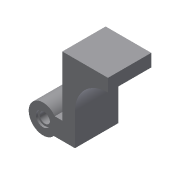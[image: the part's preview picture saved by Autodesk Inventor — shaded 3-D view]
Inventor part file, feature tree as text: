
AUTODESK INVENTOR PART (.ipt)
format: ipt  version: 2015 (Build 190159000, 159)  size: 150,016 bytes
history: native  units: in
note: dims shown in document units (in); Inventor stores cm internally (conversion verified against a paired STEP export)
features: extrude x6, sketch x6, mirror x2, projected_geometry x2, fillet x1, reference x1
ambient origin geometry x8: Origin, YZ Plane, XZ Plane, XY Plane, X Axis, Y Axis, Z Axis, Center Point
bodies: Solid1 (feature_tree)
feature tree (18):
  extrude  "Extrusion1"  Depth=0.9375in TaperAngle=0.0deg
  extrude  "Extrusion2"  Depth=0.4882in TaperAngle=0.0deg
  mirror  "Mirror1"
  extrude  "Extrusion3"  Depth=0.0591in TaperAngle=0.0deg
  extrude  "Extrusion4"  Depth=0.3831in
  mirror  "Mirror2"
  extrude  "Extrusion5"  Depth=1.0in
  fillet  "Fillet3"  Radius=1.0in
  extrude  "Extrusion6"  [1 undecoded]
  sketch  "Sketch1"  dims[d0=0.375in d1=0.0in d2=0.9375in d3=0.0in]
  reference  "Reference1"
  sketch  "Sketch2"  dims[d4=0.3125in d5=0.4882in d6=0.0in]
  sketch  "Sketch3"  dims[d7=0.4331in d8=0.0591in d9=0.0in]
  sketch  "Sketch4"  dims[d11=2.3455in d12=0.3831in]
  sketch  "Sketch7"  dims[d13=1.0in d14=0.0in d16=1.0in d17=1.0in d18=0.0in]
  projected_geometry  "Projected Loop1"
  sketch  "Sketch9"
  projected_geometry  "Projected Loop2"
note: 1 required parameter value undecoded (feature->parameter linkage not recoverable at this tier; creation-order binding heuristic only, values carry confidence <= 0.55)
